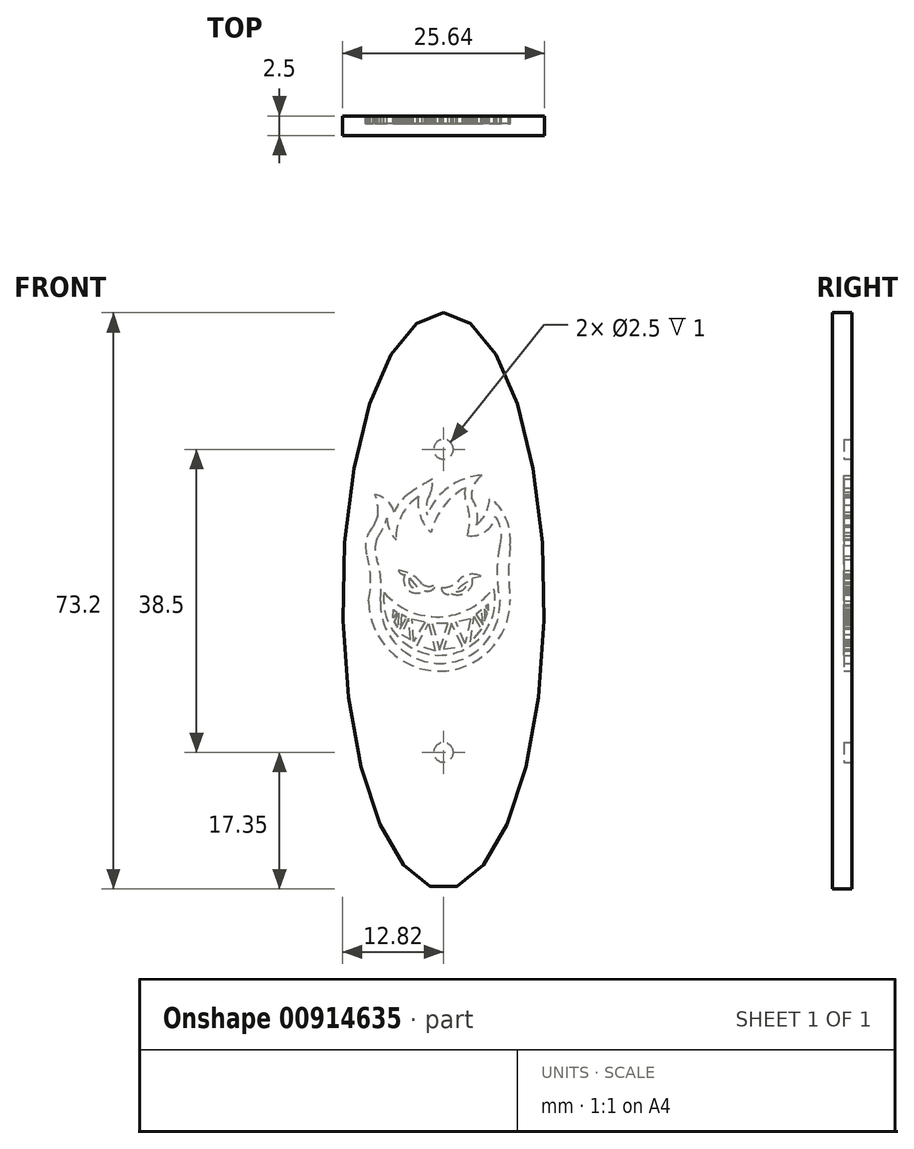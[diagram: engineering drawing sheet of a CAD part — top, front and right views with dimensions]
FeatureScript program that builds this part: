
annotation { "Feature Type Name" : "Feature", "Feature Type Description" : "" }
export const myFeature = defineFeature(function(context is Context, id is Id, definition is map)
    precondition{}
    {
        {
            var Q0;
            Q0=qCreatedBy(makeId("Front.planeOp"),FACE);
            var sketch = newSketch(context, id + "F0", { "sketchPlane" : qUnion([Q0])});
            skEllipse(sketch, "E0", {"center": v(0, 0) * mm, "majorRadius": 36.6 * mm, "minorRadius": 12.82 * mm, "majorAxis": v(0, 1)});
            skSolve(sketch);
        }
        {
            var Q0;
            Q0 = qSketchRegion(id + "F0", true);
            var Q1;
            Q1=makeQuery(id+"F0.imprint","IMPRINT",FACE,{"disambiguationData":[TD([[makeQuery(id+"F0.imprint","IMPRINT",EDGE,{"derivedFrom":sQuery(id+"F0.wireOp",EDGE,"E0")}),1.0]])]});
            extrude(context, id + "F1", {"entities" : qUnion([Q0, Q1]), "depth" : 2.5 * mm, "offsetDistance" : 25 * mm});
        }
        {
            var Q0;
            Q0=makeQuery(id+"F1.opExtrude","CAP_FACE",FACE,{"disambiguationData":[OSD([sQuery(id+"F0.wireOp",EDGE,"E0")])],"isStart":true});
            var sketch = newSketch(context, id + "F2", { "sketchPlane" : qUnion([Q0])});
            skArc(sketch, "E1", {"start": v(-8.47, 0) * mm, "mid": v(0.52, -8.92) * mm, "end": v(9.52, 0) * mm});
            skArc(sketch, "E2", {"start": v(-8.47, 0) * mm, "mid": v(-8.28, 3.52) * mm, "end": v(-8.47, 7.04) * mm});
            skArc(sketch, "E3", {"start": v(-5.86, 13.13) * mm, "mid": v(-7.95, 10.42) * mm, "end": v(-8.47, 7.04) * mm});
            skArc(sketch, "E4", {"start": v(-5.86, 13.13) * mm, "mid": v(-5.42, 11.2) * mm, "end": v(-4.22, 9.65) * mm});
            skArc(sketch, "E5", {"start": v(-3.54, 13.13) * mm, "mid": v(-4.23, 11.46) * mm, "end": v(-4.22, 9.65) * mm});
            skArc(sketch, "E6", {"start": v(-3.54, 13.13) * mm, "mid": v(-3.85, 14.72) * mm, "end": v(-4.9, 15.94) * mm});
            skArc(sketch, "E7", {"start": v(2.07, 10.88) * mm, "mid": v(-0.66, 14.44) * mm, "end": v(-4.9, 15.94) * mm});
            skArc(sketch, "E8", {"start": v(2.07, 10.88) * mm, "mid": v(2.17, 12.23) * mm, "end": v(1.71, 13.51) * mm});
            skArc(sketch, "E9", {"start": v(1.38, 15.45) * mm, "mid": v(1.44, 14.46) * mm, "end": v(1.71, 13.51) * mm});
            skArc(sketch, "E10", {"start": v(4.08, 13.84) * mm, "mid": v(2.75, 14.68) * mm, "end": v(1.38, 15.45) * mm});
            skArc(sketch, "E11", {"start": v(6.25, 11.27) * mm, "mid": v(5.37, 12.73) * mm, "end": v(4.08, 13.84) * mm});
            skArc(sketch, "E12", {"start": v(8.69, 13.51) * mm, "mid": v(7.16, 12.72) * mm, "end": v(6.25, 11.27) * mm});
            skArc(sketch, "E13", {"start": v(8.69, 13.51) * mm, "mid": v(8.36, 12.15) * mm, "end": v(8.36, 10.75) * mm});
            skLineSegment(sketch, "E14", {"start": v(8.36, 10.75) * mm, "end": v(8.95, 9.4) * mm});
            skArc(sketch, "E15", {"start": v(9.67, 5.68) * mm, "mid": v(9.84, 7.64) * mm, "end": v(8.95, 9.4) * mm});
            skArc(sketch, "E16", {"start": v(9.67, 5.68) * mm, "mid": v(9.25, 2.85) * mm, "end": v(9.52, 0) * mm});
            skArc(sketch, "E17", {"start": v(-7.17, 0) * mm, "mid": v(0.43, -7.94) * mm, "end": v(8.02, 0) * mm});
            skArc(sketch, "E18", {"start": v(-7.17, 0) * mm, "mid": v(-6.8, 3.52) * mm, "end": v(-7.17, 7.04) * mm});
            skArc(sketch, "E19", {"start": v(-6.59, 10.76) * mm, "mid": v(-7.3, 8.96) * mm, "end": v(-7.17, 7.04) * mm});
            skArc(sketch, "E20", {"start": v(-6.59, 10.76) * mm, "mid": v(-5.31, 8.8) * mm, "end": v(-3.03, 8.3) * mm});
            skArc(sketch, "E21", {"start": v(-3.03, 12.16) * mm, "mid": v(-3.32, 10.23) * mm, "end": v(-3.03, 8.3) * mm});
            skArc(sketch, "E22", {"start": v(-3.03, 12.16) * mm, "mid": v(-2.72, 13.24) * mm, "end": v(-2.78, 14.36) * mm});
            skArc(sketch, "E23", {"start": v(1.57, 8.66) * mm, "mid": v(0, 11.97) * mm, "end": v(-2.78, 14.36) * mm});
            skArc(sketch, "E24", {"start": v(1.57, 8.66) * mm, "mid": v(2.94, 10.77) * mm, "end": v(3.19, 13.27) * mm});
            skArc(sketch, "E25", {"start": v(6.05, 7.75) * mm, "mid": v(5.31, 10.87) * mm, "end": v(3.19, 13.27) * mm});
            skArc(sketch, "E26", {"start": v(6.05, 7.75) * mm, "mid": v(6.85, 9.03) * mm, "end": v(7.2, 10.5) * mm});
            skArc(sketch, "E27", {"start": v(7.2, 10.5) * mm, "mid": v(7.73, 9.15) * mm, "end": v(8.45, 7.89) * mm});
            skArc(sketch, "E28", {"start": v(8.45, 5.28) * mm, "mid": v(8.69, 6.58) * mm, "end": v(8.45, 7.89) * mm});
            skArc(sketch, "E29", {"start": v(8.45, 5.28) * mm, "mid": v(7.95, 2.66) * mm, "end": v(8.02, 0) * mm});
            skArc(sketch, "E30", {"start": v(5.73, 3.86) * mm, "mid": v(4.04, 3.33) * mm, "end": v(2.72, 2.13) * mm});
            skArc(sketch, "E31", {"start": v(0.94, 2.13) * mm, "mid": v(1.83, 1.85) * mm, "end": v(2.72, 2.13) * mm});
            skArc(sketch, "E32", {"start": v(0.94, 2.13) * mm, "mid": v(1.5, 1.36) * mm, "end": v(2.43, 1.29) * mm});
            skArc(sketch, "E33", {"start": v(2.43, 1.29) * mm, "mid": v(4.45, 1.35) * mm, "end": v(4.9, 3.33) * mm});
            skArc(sketch, "E34", {"start": v(4.9, 3.33) * mm, "mid": v(5.4, 3.45) * mm, "end": v(5.73, 3.86) * mm});
            skLineSegment(sketch, "E35", {"start": v(4.33, 2.88) * mm, "end": v(3.19, 1.56) * mm});
            skArc(sketch, "E36", {"start": v(3.19, 1.56) * mm, "mid": v(4.14, 1.89) * mm, "end": v(4.33, 2.88) * mm});
            skArc(sketch, "E37", {"start": v(-3.02, 2.39) * mm, "mid": v(-2.57, 1.47) * mm, "end": v(-1.58, 1.22) * mm});
            skArc(sketch, "E38", {"start": v(-1.58, 1.22) * mm, "mid": v(-2.24, 1.87) * mm, "end": v(-3.02, 2.39) * mm});
            skArc(sketch, "E39", {"start": v(-1.8, 2.42) * mm, "mid": v(-3.15, 3.33) * mm, "end": v(-4.77, 3.12) * mm});
            skArc(sketch, "E40", {"start": v(-1.8, 2.42) * mm, "mid": v(-0.84, 1.85) * mm, "end": v(0.27, 1.68) * mm});
            skArc(sketch, "E41", {"start": v(-0.97, 0.94) * mm, "mid": v(-0.13, 0.94) * mm, "end": v(0.27, 1.68) * mm});
            skArc(sketch, "E42", {"start": v(-3.68, 2.13) * mm, "mid": v(-2.59, 0.93) * mm, "end": v(-0.97, 0.94) * mm});
            skLineSegment(sketch, "E43", {"start": v(-3.68, 2.13) * mm, "end": v(-3.68, 2.82) * mm});
            skLineSegment(sketch, "E44", {"start": v(-4.77, 3.12) * mm, "end": v(-3.68, 2.82) * mm});
            skArc(sketch, "E45", {"start": v(-6.4, 1.7) * mm, "mid": v(0.42, -2.02) * mm, "end": v(7.55, 1.07) * mm});
            skArc(sketch, "E46", {"start": v(-6.4, 1.7) * mm, "mid": v(0.2, -6.9) * mm, "end": v(7.55, 1.07) * mm});
            skLineSegment(sketch, "E47", {"start": v(6.37, -1.09) * mm, "end": v(5.88, -1.47) * mm});
            skLineSegment(sketch, "E48", {"start": v(5.88, -1.47) * mm, "end": v(6.4, -2.15) * mm});
            skLineSegment(sketch, "E49", {"start": v(6.4, -2.15) * mm, "end": v(6.37, -1.09) * mm});
            skLineSegment(sketch, "E50", {"start": v(5.68, -1.56) * mm, "end": v(5.8, -3.35) * mm});
            skLineSegment(sketch, "E51", {"start": v(5.8, -3.35) * mm, "end": v(6.25, -2.66) * mm});
            skLineSegment(sketch, "E52", {"start": v(6.25, -2.66) * mm, "end": v(5.68, -1.56) * mm});
            skLineSegment(sketch, "E53", {"start": v(5.33, -1.72) * mm, "end": v(5.5, -3.56) * mm});
            skLineSegment(sketch, "E54", {"start": v(5.5, -3.56) * mm, "end": v(4.68, -2.14) * mm});
            skLineSegment(sketch, "E55", {"start": v(4.68, -2.14) * mm, "end": v(5.33, -1.72) * mm});
            skLineSegment(sketch, "E56", {"start": v(5.33, -4.26) * mm, "end": v(4.2, -4.9) * mm});
            skLineSegment(sketch, "E57", {"start": v(4.2, -4.9) * mm, "end": v(4.44, -2.26) * mm});
            skLineSegment(sketch, "E58", {"start": v(4.44, -2.26) * mm, "end": v(5.33, -4.26) * mm});
            skLineSegment(sketch, "E59", {"start": v(3.97, -2.31) * mm, "end": v(2.34, -2.65) * mm});
            skLineSegment(sketch, "E60", {"start": v(2.34, -2.65) * mm, "end": v(3.8, -5.19) * mm});
            skLineSegment(sketch, "E61", {"start": v(3.8, -5.19) * mm, "end": v(3.97, -2.31) * mm});
            skLineSegment(sketch, "E62", {"start": v(1.9, -2.9) * mm, "end": v(1.05, -6.35) * mm});
            skLineSegment(sketch, "E63", {"start": v(1.05, -6.35) * mm, "end": v(3.35, -5.67) * mm});
            skLineSegment(sketch, "E64", {"start": v(3.35, -5.67) * mm, "end": v(1.9, -2.9) * mm});
            skLineSegment(sketch, "E65", {"start": v(1.46, -2.9) * mm, "end": v(0.49, -6.21) * mm});
            skLineSegment(sketch, "E66", {"start": v(0.49, -6.21) * mm, "end": v(-0.58, -2.9) * mm});
            skLineSegment(sketch, "E67", {"start": v(-0.58, -2.9) * mm, "end": v(1.46, -2.9) * mm});
            skLineSegment(sketch, "E68", {"start": v(-1.03, -2.9) * mm, "end": v(0, -6.13) * mm});
            skLineSegment(sketch, "E69", {"start": v(0, -6.13) * mm, "end": v(-2.39, -5.76) * mm});
            skLineSegment(sketch, "E70", {"start": v(-2.39, -5.76) * mm, "end": v(-1.03, -2.9) * mm});
            skLineSegment(sketch, "E71", {"start": v(-3.43, -2.31) * mm, "end": v(-2.72, -5.43) * mm});
            skLineSegment(sketch, "E72", {"start": v(-2.72, -5.43) * mm, "end": v(-1.56, -2.7) * mm});
            skLineSegment(sketch, "E73", {"start": v(-3.43, -2.31) * mm, "end": v(-1.56, -2.7) * mm});
            skLineSegment(sketch, "E74", {"start": v(-3.89, -2) * mm, "end": v(-4.8, -3.6) * mm});
            skLineSegment(sketch, "E75", {"start": v(-4.8, -3.6) * mm, "end": v(-3.43, -5.23) * mm});
            skLineSegment(sketch, "E76", {"start": v(-3.43, -5.23) * mm, "end": v(-3.89, -2) * mm});
            skLineSegment(sketch, "E77", {"start": v(-4.86, -1.19) * mm, "end": v(-4.1, -1.72) * mm});
            skLineSegment(sketch, "E78", {"start": v(-4.1, -1.72) * mm, "end": v(-5.04, -3.04) * mm});
            skLineSegment(sketch, "E79", {"start": v(-5.04, -3.04) * mm, "end": v(-4.86, -1.19) * mm});
            skLineSegment(sketch, "E80", {"start": v(-5.2, -1.01) * mm, "end": v(-5.2, -2.57) * mm});
            skLineSegment(sketch, "E81", {"start": v(-5.2, -2.57) * mm, "end": v(-5.56, -1.53) * mm});
            skLineSegment(sketch, "E82", {"start": v(-5.56, -1.53) * mm, "end": v(-5.2, -1.01) * mm});
            skLineSegment(sketch, "E83", {"start": v(-5.32, -0.73) * mm, "end": v(-5.7, -1.23) * mm});
            skLineSegment(sketch, "E84", {"start": v(-5.7, -1.23) * mm, "end": v(-5.7, -0.46) * mm});
            skLineSegment(sketch, "E85", {"start": v(-5.7, -0.46) * mm, "end": v(-5.32, -0.73) * mm});
            skSolve(sketch);
        }
        {
            var Q0;
            Q0 = qSketchRegion(id + "F2", true);
            var Q1;
            Q1=makeQuery(id+"F1.opExtrude","CAP_FACE",FACE,{"disambiguationData":[OSD([sQuery(id+"F0.wireOp",EDGE,"E0")])],"isStart":false});
            var Q2;
            Q2=makeQuery(id+"F2.imprint","IMPRINT",FACE,{"disambiguationData":[TD([[makeQuery(id+"F2.imprint","IMPRINT",EDGE,{"derivedFrom":sQuery(id+"F2.wireOp",EDGE,"E45")}),-1.0]])]});
            var Q3;
            Q3=makeQuery(id+"F2.imprint","IMPRINT",FACE,{"disambiguationData":[TD([[makeQuery(id+"F2.imprint","IMPRINT",EDGE,{"derivedFrom":sQuery(id+"F2.wireOp",EDGE,"E37")}),-1.0]])]});
            var Q4;
            Q4=makeQuery(id+"F2.imprint","IMPRINT",FACE,{"disambiguationData":[TD([[makeQuery(id+"F2.imprint","IMPRINT",EDGE,{"derivedFrom":sQuery(id+"F2.wireOp",EDGE,"E30")}),1.0]])]});
            extrude(context, id + "F3", {"entities" : qUnion([Q0, Q1, Q2, Q3, Q4]), "operationType" : NewBodyOperationType.REMOVE, "oppositeDirection" : true, "depth" : 1 * mm, "offsetDistance" : 25 * mm});
        }
        {
            var Q0;
            {var subQ0=sQuery(id+"F0.wireOp",EDGE,"E0");Q0=makeQuery(id+"F3.boolean.opBoolean","SPLIT",FACE,{"disambiguationData":[TD([makeQuery(id+"F1.opExtrude","SWEPT_FACE",FACE,{"disambiguationData":[OSD([subQ0])]})])],"derivedFrom":makeQuery(id+"F1.opExtrude","CAP_FACE",FACE,{"disambiguationData":[OSD([subQ0])],"isStart":true})});}
            var sketch = newSketch(context, id + "F4", { "sketchPlane" : qUnion([Q0])});
            skCircle(sketch, "E86", {"center": v(0, 19.25) * mm, "radius": 1.25 * mm});
            skCircle(sketch, "E87", {"center": v(0, -19.25) * mm, "radius": 1.25 * mm});
            skSolve(sketch);
        }
        {
            var Q0;
            Q0 = qSketchRegion(id + "F4", true);
            extrude(context, id + "F5", {"entities" : qUnion([Q0]), "operationType" : NewBodyOperationType.REMOVE, "oppositeDirection" : true, "depth" : 1 * mm, "offsetDistance" : 25 * mm});
        }
    });
